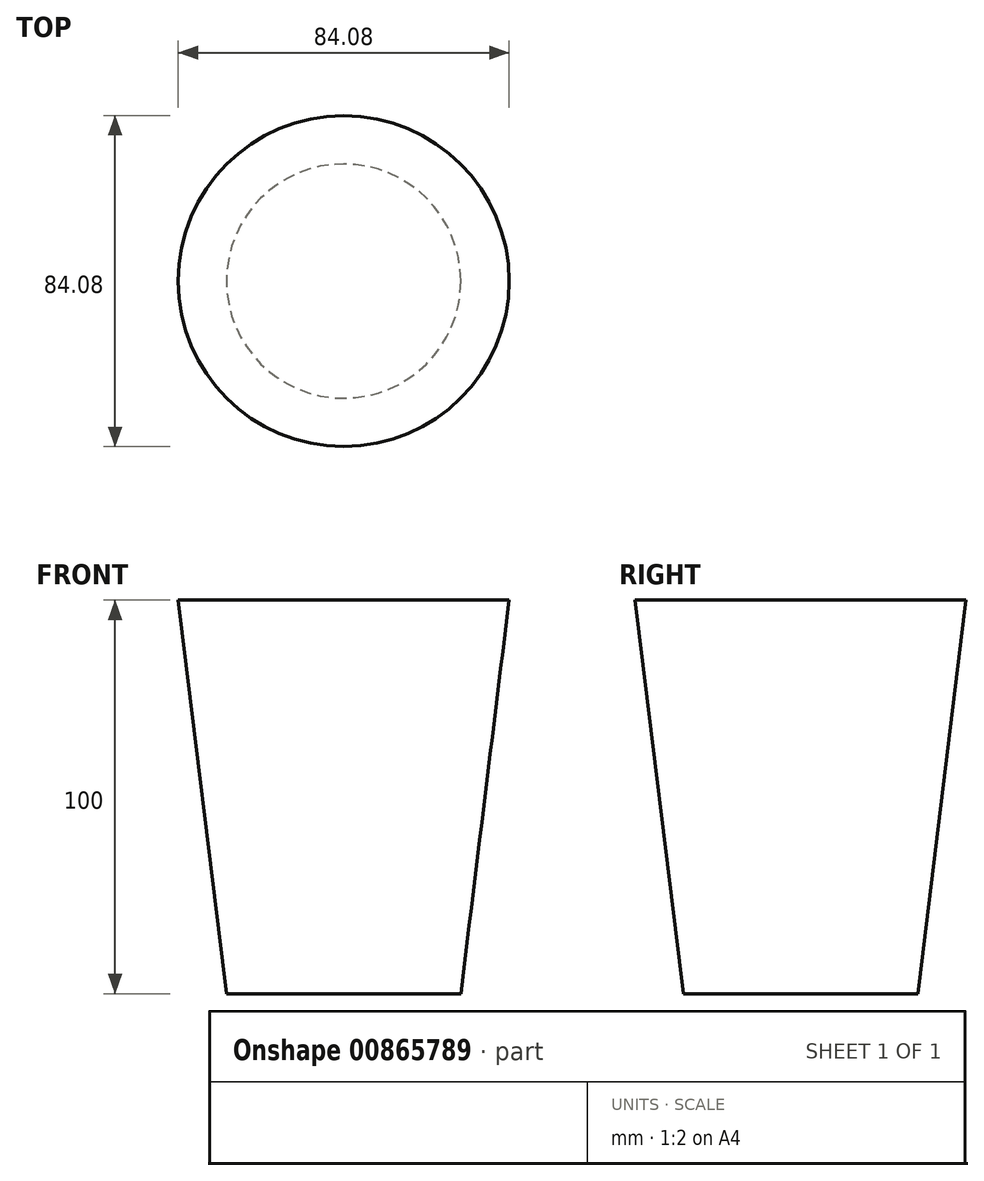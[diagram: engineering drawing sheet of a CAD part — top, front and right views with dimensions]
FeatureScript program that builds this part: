
annotation { "Feature Type Name" : "Feature", "Feature Type Description" : "" }
export const myFeature = defineFeature(function(context is Context, id is Id, definition is map)
    precondition{}
    {
        {
            var Q0;
            Q0=qCreatedBy(makeId("Top.planeOp"),FACE);
            var sketch = newSketch(context, id + "F0", { "sketchPlane" : qUnion([Q0])});
            skCircle(sketch, "E0", {"center": v(0, 0) * mm, "radius": 42.04 * mm});
            skSolve(sketch);
        }
        {
            var Q0;
            Q0=makeQuery(id+"F0.imprint","IMPRINT",FACE,{"disambiguationData":[TD([[makeQuery(id+"F0.imprint","IMPRINT",EDGE,{"derivedFrom":sQuery(id+"F0.wireOp",EDGE,"E0")}),1.0]])]});
            extrude(context, id + "F1", {"entities" : qUnion([Q0]), "oppositeDirection" : true, "depth" : 100 * mm, "offsetDistance" : 25 * mm, "hasDraft" : true, "draftAngle" : 7 * degree, "draftPullDirection" : true});
        }
    });
